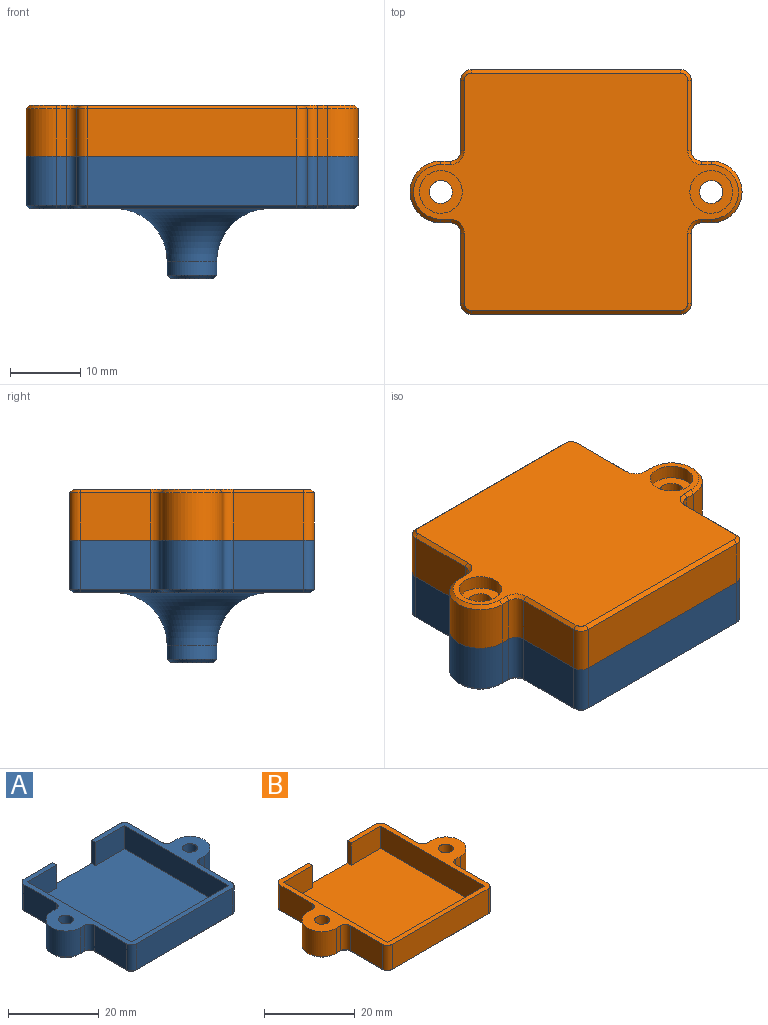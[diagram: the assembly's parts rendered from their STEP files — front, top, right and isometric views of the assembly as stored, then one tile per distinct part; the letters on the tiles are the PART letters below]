
ASSEMBLY  parts=2 mates=1
PART A: 72 faces, bbox 47.4x34.9x20.3 mm
  f0: plane 46.4x33.9mm, normal (0,0,-1), area 744.2mm2, adj f32,f33,f34,f35,f36,f37,f39,f40
  f1: plane 29.9x7mm, normal (0,1,0), area 133.7mm2, adj f2,f6,f7,f25,f26,f31,f69
  f2: plane 33.65x30.4mm, normal (0,0,1), area 1000.1mm2, adj f1,f3,f4,f5,f6,f26,f27,f29
  f3: plane 32.4x6.25mm, normal (1,0,0), area 202.5mm2, adj f2,f4,f29,f31
  f4: plane 30.4x6.25mm, normal (0,1,0), area 190mm2, adj f2,f3,f5,f31
  f5: plane 32.4x6.25mm, normal (-1,0,0), area 202.5mm2, adj f2,f4,f27,f31
  f6: plane 6.25x1.25mm, normal (1,0,0), area 7.8mm2, adj f1,f2,f29,f31
  f7: cylinder r=1.5mm len=7mm, axis (0,0,-1), area 16.5mm2, adj f1,f8,f31,f68
  f8: plane 10.05x7mm, normal (-1,0,0), area 70.3mm2, adj f7,f9,f31,f66
  f9: cylinder r=1.5mm len=7mm, axis (0,0,-1), area 16.5mm2, adj f8,f10,f31,f64
  f10: plane 7x1.35mm, normal (0,1,0), area 9.5mm2, adj f9,f11,f31,f62
  f11: cylinder r=4.4mm len=8.8mm, axis (0,0,-1), area 96.8mm2, adj f10,f12,f31,f60
  f12: plane 7x1.35mm, normal (0,-1,0), area 9.5mm2, adj f11,f13,f31,f58
  f13: cylinder r=1.5mm len=7mm, axis (0,0,-1), area 16.5mm2, adj f12,f14,f31,f56
  f14: plane 10.05x7mm, normal (-1,0,0), area 70.3mm2, adj f13,f15,f31,f54
  f15: cylinder r=1.5mm len=7mm, axis (0,0,-1), area 16.5mm2, adj f14,f16,f31,f52
  f16: plane 29.9x7mm, normal (0,-1,0), area 209.3mm2, adj f15,f17,f31,f50
  f17: cylinder r=1.5mm len=7mm, axis (0,0,-1), area 16.5mm2, adj f16,f18,f31,f51
  f18: plane 10.05x7mm, normal (1,0,0), area 70.3mm2, adj f17,f19,f31,f53
  f19: cylinder r=1.5mm len=7mm, axis (0,0,-1), area 16.5mm2, adj f18,f20,f31,f55
  f20: plane 7x1.35mm, normal (0,-1,0), area 9.5mm2, adj f19,f21,f31,f57
  f21: cylinder r=4.4mm len=8.8mm, axis (0,0,-1), area 96.8mm2, adj f20,f22,f31,f59
  f22: plane 7x1.35mm, normal (0,1,0), area 9.5mm2, adj f21,f23,f31,f61
  f23: cylinder r=1.5mm len=7mm, axis (0,0,-1), area 16.5mm2, adj f22,f24,f31,f63
  f24: plane 10.05x7mm, normal (1,0,0), area 70.3mm2, adj f23,f25,f31,f65
  f25: cylinder r=1.5mm len=7mm, axis (0,0,-1), area 16.5mm2, adj f1,f24,f31,f67
  f26: plane 6.25x1.25mm, normal (-1,0,0), area 7.8mm2, adj f1,f2,f27,f31
  f27: plane 9.15x6.25mm, normal (0,-1,0), area 57.2mm2, adj f2,f5,f26,f31
  f28: cylinder r=1.65mm len=4mm, axis (0,0,-1), area 41.5mm2, adj f31,f45
  f29: plane 9.15x6.25mm, normal (0,-1,0), area 57.2mm2, adj f2,f3,f6,f31
  f30: cylinder r=1.65mm len=4mm, axis (0,0,-1), area 41.5mm2, adj f31,f38
  f31: plane 47.4x34.9mm, normal (0,0,1), area 242mm2, adj f1,f3,f4,f5,f6,f7,f8,f9
  f32: plane 3.5x3.29mm, normal (-1,0,0), area 11.5mm2, adj f0,f33,f37,f38
  f33: plane 3.5x2.85mm, normal (-0.5,-0.87,0), area 11.5mm2, adj f0,f32,f34,f38
  f34: plane 3.5x2.85mm, normal (0.5,-0.87,0), area 11.5mm2, adj f0,f33,f35,f38
  f35: plane 3.5x3.29mm, normal (1,0,0), area 11.5mm2, adj f0,f34,f36,f38
  f36: plane 3.5x2.85mm, normal (0.5,0.87,0), area 11.5mm2, adj f0,f35,f37,f38
  f37: plane 3.5x2.85mm, normal (-0.5,0.87,0), area 11.5mm2, adj f0,f32,f36,f38
  f38: plane 6.58x5.7mm, normal (0,0,-1), area 19.6mm2, adj f30,f32,f33,f34,f35,f36,f37
  f39: plane 3.5x3.29mm, normal (-1,0,0), area 11.5mm2, adj f0,f40,f44,f45
  f40: plane 3.5x2.85mm, normal (-0.5,-0.87,0), area 11.5mm2, adj f0,f39,f41,f45
  f41: plane 3.5x2.85mm, normal (0.5,-0.87,0), area 11.5mm2, adj f0,f40,f42,f45
  f42: plane 3.5x3.29mm, normal (1,0,0), area 11.5mm2, adj f0,f41,f43,f45
  f43: plane 3.5x2.85mm, normal (0.5,0.87,0), area 11.5mm2, adj f0,f42,f44,f45
  f44: plane 3.5x2.85mm, normal (-0.5,0.87,0), area 11.5mm2, adj f0,f39,f43,f45
  f45: plane 6.58x5.7mm, normal (0,0,-1), area 19.6mm2, adj f28,f39,f40,f41,f42,f43,f44
  f46: cylinder r=2.05mm len=10mm, axis (0,0,1), area 128.8mm2, adj f48,f49
  f47: cylinder r=3.55mm len=7.1mm, axis (0,0,1), area 44.6mm2, adj f70,f71
  f48: plane 6.1x6.1mm, normal (0,0,-1), area 16mm2, adj f46,f70
  f49: plane 4.1x4.1mm, normal (0,0,-1), area 13.2mm2, adj f46
  f50: plane 29.9x0.5mm, normal (0,-0.71,-0.71), area 21.1mm2, adj f0,f16,f51,f52
  f51: cone r=1.5mm half-angle=45deg, axis (0,0,1), area 1.4mm2, adj f0,f17,f50,f53
  f52: cone r=1.5mm half-angle=45deg, axis (0,0,1), area 1.4mm2, adj f0,f15,f50,f54
  f53: plane 10.05x0.5mm, normal (0.71,0,-0.71), area 7.1mm2, adj f0,f18,f51,f55
  f54: plane 10.05x0.5mm, normal (-0.71,0,-0.71), area 7.1mm2, adj f0,f14,f52,f56
  f55: cone r=1.5mm half-angle=45deg, axis (0,0,-1), area 1.9mm2, adj f0,f19,f53,f57
  f56: cone r=2mm half-angle=45deg, axis (0,0,-1), area 1.9mm2, adj f0,f13,f54,f58
  f57: plane 1.35x0.5mm, normal (0,-0.71,-0.71), area 1mm2, adj f0,f20,f55,f59
  f58: plane 1.35x0.5mm, normal (0,-0.71,-0.71), area 1mm2, adj f0,f12,f56,f60
  f59: cone r=3.9mm half-angle=45deg, axis (0,0,1), area 9.2mm2, adj f0,f21,f57,f61
  f60: cone r=4.4mm half-angle=45deg, axis (0,0,1), area 9.2mm2, adj f0,f11,f58,f62
  f61: plane 1.35x0.5mm, normal (0,0.71,-0.71), area 1mm2, adj f0,f22,f59,f63
  f62: plane 1.35x0.5mm, normal (0,0.71,-0.71), area 1mm2, adj f0,f10,f60,f64
  f63: cone r=1.5mm half-angle=45deg, axis (0,0,-1), area 1.9mm2, adj f0,f23,f61,f65
  f64: cone r=2mm half-angle=45deg, axis (0,0,-1), area 1.9mm2, adj f0,f9,f62,f66
  f65: plane 10.05x0.5mm, normal (0.71,0,-0.71), area 7.1mm2, adj f0,f24,f63,f67
  f66: plane 10.05x0.5mm, normal (-0.71,0,-0.71), area 7.1mm2, adj f0,f8,f64,f68
  f67: cone r=1.5mm half-angle=45deg, axis (0,0,1), area 1.4mm2, adj f0,f25,f65,f69
  f68: cone r=1.5mm half-angle=45deg, axis (0,0,1), area 1.4mm2, adj f0,f7,f66,f69
  f69: plane 29.9x0.5mm, normal (0,0.71,-0.71), area 21.1mm2, adj f0,f1,f67,f68
  f70: cone r=3.55mm half-angle=45deg, axis (0,0,1), area 14.7mm2, adj f47,f48
  f71: torus R=11.05mm, axis (0,0,1), area 464.5mm2, adj f0,f47
PART B: 56 faces, bbox 47.4x34.9x7.3 mm
  f0: plane 46.4x33.9mm, normal (0,0,-1), area 1125.6mm2, adj f32,f34,f36,f37,f38,f39,f40,f41
  f1: cylinder r=1.65mm len=5.25mm, axis (0,0,-1), area 54.4mm2, adj f31,f35
  f2: cylinder r=1.65mm len=5.25mm, axis (0,0,-1), area 54.4mm2, adj f31,f33
  f3: plane 29.9x6.75mm, normal (0,1,0), area 129.2mm2, adj f4,f8,f9,f27,f28,f31,f39
  f4: plane 33.65x30.4mm, normal (0,0,1), area 1000.1mm2, adj f3,f5,f6,f7,f8,f28,f29,f30
  f5: plane 32.4x6mm, normal (1,0,0), area 194.4mm2, adj f4,f6,f30,f31
  f6: plane 30.4x6mm, normal (0,1,0), area 182.4mm2, adj f4,f5,f7,f31
  f7: plane 32.4x6mm, normal (-1,0,0), area 194.4mm2, adj f4,f6,f29,f31
  f8: plane 6x1.25mm, normal (1,0,0), area 7.5mm2, adj f3,f4,f30,f31
  f9: cylinder r=1.5mm len=6.75mm, axis (0,0,-1), area 15.9mm2, adj f3,f10,f31,f41
  f10: plane 10.05x6.75mm, normal (-1,0,0), area 67.8mm2, adj f9,f11,f31,f43
  f11: cylinder r=1.5mm len=6.75mm, axis (0,0,-1), area 15.9mm2, adj f10,f12,f31,f45
  f12: plane 6.75x1.35mm, normal (0,1,0), area 9.1mm2, adj f11,f13,f31,f47
  f13: cylinder r=4.4mm len=8.8mm, axis (0,0,-1), area 93.3mm2, adj f12,f14,f31,f49
  f14: plane 6.75x1.35mm, normal (0,-1,0), area 9.1mm2, adj f13,f15,f31,f51
  f15: cylinder r=1.5mm len=6.75mm, axis (0,0,-1), area 15.9mm2, adj f14,f16,f31,f53
  f16: plane 10.05x6.75mm, normal (-1,0,0), area 67.8mm2, adj f15,f17,f31,f55
  f17: cylinder r=1.5mm len=6.75mm, axis (0,0,-1), area 15.9mm2, adj f16,f18,f31,f54
  f18: plane 29.9x6.75mm, normal (0,-1,0), area 201.8mm2, adj f17,f19,f31,f52
  f19: cylinder r=1.5mm len=6.75mm, axis (0,0,-1), area 15.9mm2, adj f18,f20,f31,f50
  f20: plane 10.05x6.75mm, normal (1,0,0), area 67.8mm2, adj f19,f21,f31,f48
  f21: cylinder r=1.5mm len=6.75mm, axis (0,0,-1), area 15.9mm2, adj f20,f22,f31,f46
  f22: plane 6.75x1.35mm, normal (0,-1,0), area 9.1mm2, adj f21,f23,f31,f44
  f23: cylinder r=4.4mm len=8.8mm, axis (0,0,-1), area 93.3mm2, adj f22,f24,f31,f42
  f24: plane 6.75x1.35mm, normal (0,1,0), area 9.1mm2, adj f23,f25,f31,f40
  f25: cylinder r=1.5mm len=6.75mm, axis (0,0,-1), area 15.9mm2, adj f24,f26,f31,f38
  f26: plane 10.05x6.75mm, normal (1,0,0), area 67.8mm2, adj f25,f27,f31,f36
  f27: cylinder r=1.5mm len=6.75mm, axis (0,0,-1), area 15.9mm2, adj f3,f26,f31,f37
  f28: plane 6x1.25mm, normal (-1,0,0), area 7.5mm2, adj f3,f4,f29,f31
  f29: plane 9.15x6mm, normal (0,-1,0), area 54.9mm2, adj f4,f7,f28,f31
  f30: plane 9.15x6mm, normal (0,-1,0), area 54.9mm2, adj f4,f5,f8,f31
  f31: plane 47.4x34.9mm, normal (0,0,1), area 242mm2, adj f1,f2,f3,f5,f6,f7,f8,f9
  f32: cylinder r=3.05mm len=6.1mm, axis (0,0,-1), area 38.3mm2, adj f0,f33
  f33: plane 6.1x6.1mm, normal (0,0,-1), area 20.7mm2, adj f2,f32
  f34: cylinder r=3.05mm len=6.1mm, axis (0,0,-1), area 38.3mm2, adj f0,f35
  f35: plane 6.1x6.1mm, normal (0,0,-1), area 20.7mm2, adj f1,f34
  f36: plane 10.05x0.5mm, normal (0.71,0,-0.71), area 7.1mm2, adj f0,f26,f37,f38
  f37: cone r=1.5mm half-angle=45deg, axis (0,0,1), area 1.4mm2, adj f0,f27,f36,f39
  f38: cone r=1.5mm half-angle=45deg, axis (0,0,-1), area 1.9mm2, adj f0,f25,f36,f40
  f39: plane 29.9x0.5mm, normal (0,0.71,-0.71), area 21.1mm2, adj f0,f3,f37,f41
  f40: plane 1.35x0.5mm, normal (0,0.71,-0.71), area 1mm2, adj f0,f24,f38,f42
  f41: cone r=1.5mm half-angle=45deg, axis (0,0,1), area 1.4mm2, adj f0,f9,f39,f43
  f42: cone r=3.9mm half-angle=45deg, axis (0,0,1), area 9.2mm2, adj f0,f23,f40,f44
  f43: plane 10.05x0.5mm, normal (-0.71,0,-0.71), area 7.1mm2, adj f0,f10,f41,f45
  f44: plane 1.35x0.5mm, normal (0,-0.71,-0.71), area 1mm2, adj f0,f22,f42,f46
  f45: cone r=2mm half-angle=45deg, axis (0,0,-1), area 1.9mm2, adj f0,f11,f43,f47
  f46: cone r=1.5mm half-angle=45deg, axis (0,0,-1), area 1.9mm2, adj f0,f21,f44,f48
  f47: plane 1.35x0.5mm, normal (0,0.71,-0.71), area 1mm2, adj f0,f12,f45,f49
  f48: plane 10.05x0.5mm, normal (0.71,0,-0.71), area 7.1mm2, adj f0,f20,f46,f50
  f49: cone r=4.4mm half-angle=45deg, axis (0,0,1), area 9.2mm2, adj f0,f13,f47,f51
  f50: cone r=1.5mm half-angle=45deg, axis (0,0,1), area 1.4mm2, adj f0,f19,f48,f52
  f51: plane 1.35x0.5mm, normal (0,-0.71,-0.71), area 1mm2, adj f0,f14,f49,f53
  f52: plane 29.9x0.5mm, normal (0,-0.71,-0.71), area 21.1mm2, adj f0,f18,f50,f54
  f53: cone r=2mm half-angle=45deg, axis (0,0,-1), area 1.9mm2, adj f0,f15,f51,f55
  f54: cone r=1.5mm half-angle=45deg, axis (0,0,1), area 1.4mm2, adj f0,f17,f52,f55
  f55: plane 10.05x0.5mm, normal (-0.71,0,-0.71), area 7.1mm2, adj f0,f16,f53,f54
PLACE A t=(0,0,-0.25)mm
PLACE B rot(axis=(0,-1,0),180deg) t=(0,0,14.5)mm
MATE fastened B.f1 <-> A.f30  axis (0,0,-1) through (-19.3,0,7.25)mm
